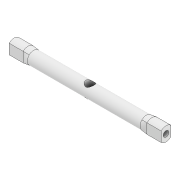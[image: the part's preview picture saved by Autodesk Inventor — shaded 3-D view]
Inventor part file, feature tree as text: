
AUTODESK INVENTOR PART (.ipt)
format: ipt  version: 2022 (Build 260153000, 153)  size: 141,312 bytes
history: native  units: mm
features: sketch x4, extrude x2, plane x2, hole x2, other x2, loft x1, mirror x1
ambient origin geometry x8: Origin, YZ Plane, XZ Plane, XY Plane, X Axis, Y Axis, Z Axis, Center Point
bodies: Solid1 (feature_tree)
feature tree (14):
  extrude  "Extrusion1"  Depth=5.0mm
  plane  "Work Plane1"
  extrude  "Extrusion3"  Depth=2.0mm
  loft  "Loft1"
  hole  "Hole1"  [1 undecoded]
  mirror  "Mirror1"
  plane  "Work Plane2"
  hole  "Hole2"  [1 undecoded]
  sketch  "Sketch1"  dims[d2=0.0mm d23=5.0mm]
  sketch  "Sketch3"  dims[d25=5.0mm d26=0.0mm d29=2.0mm]
  other  "Edges1"
  other  "Edges2"
  sketch  "Sketch4"  dims[d30=0.0mm d31=90.0deg d32=0.0mm d33=90.0deg]
  sketch  "Sketch5"  dims[d34=3.5mm d35=2.0mm d36=6.0mm d37=4.0mm d38=2.0mm d39=90.0deg d40=6.0mm d41=0.0mm d42=5.0mm d43=3.0mm d44=6.0mm d45=6.0mm d46=2.0mm d47=90.0deg d48=8.0mm d49=20.594885mm]
note: 2 required parameter values undecoded (feature->parameter linkage not recoverable at this tier; creation-order binding heuristic only, values carry confidence <= 0.55)
